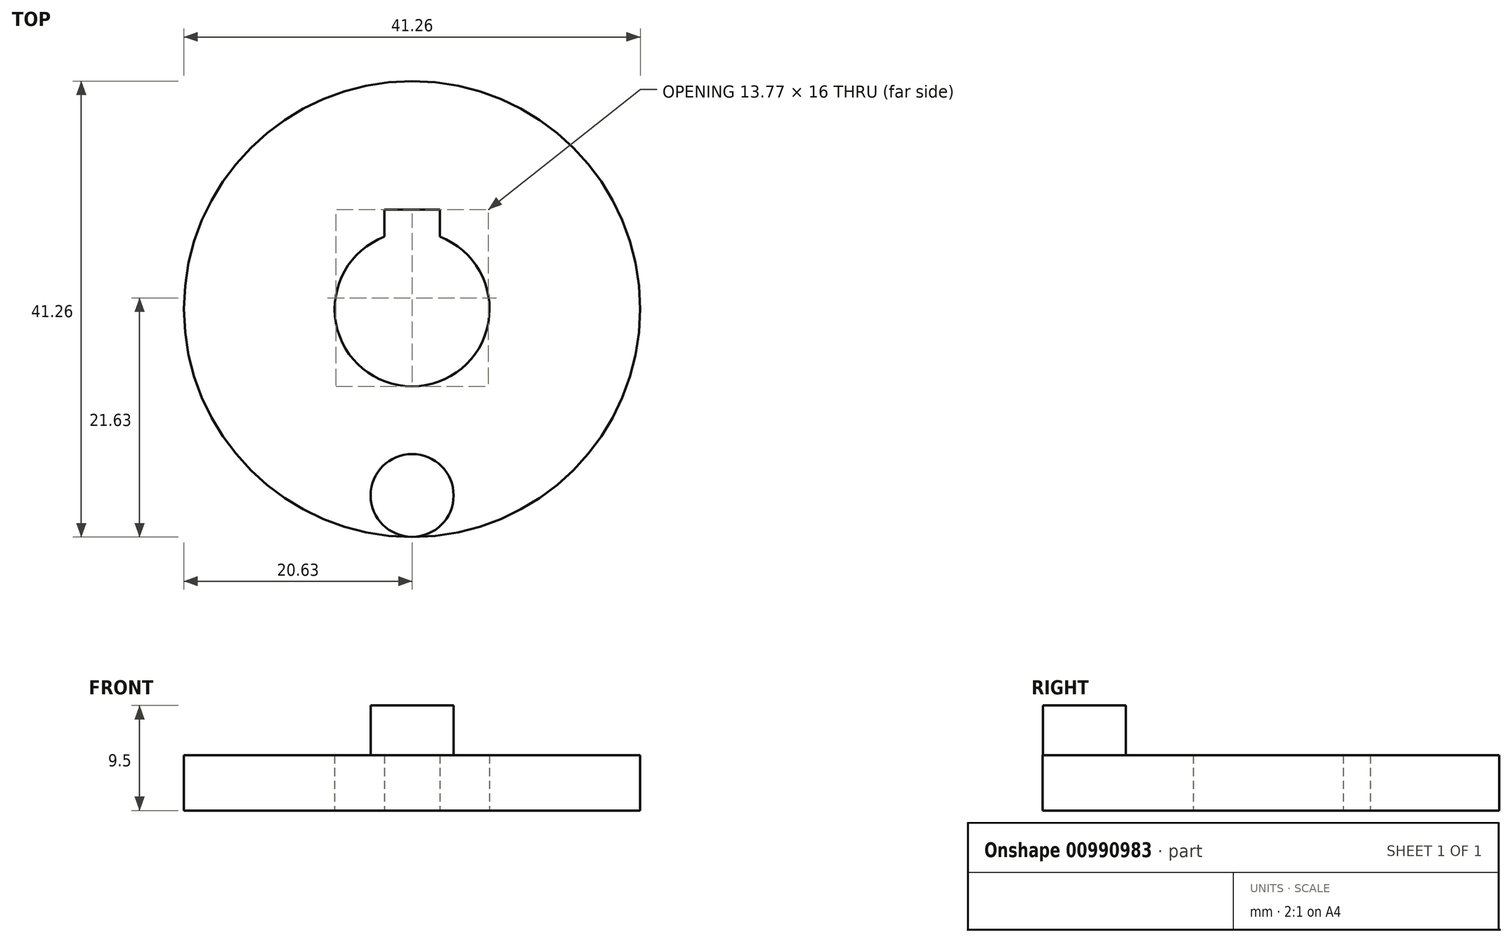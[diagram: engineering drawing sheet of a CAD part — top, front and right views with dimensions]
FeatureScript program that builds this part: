
annotation { "Feature Type Name" : "Feature", "Feature Type Description" : "" }
export const myFeature = defineFeature(function(context is Context, id is Id, definition is map)
    precondition{}
    {
        {
            var Q0;
            Q0=qCreatedBy(makeId("Top.planeOp"),FACE);
            var sketch = newSketch(context, id + "F0", { "sketchPlane" : qUnion([Q0])});
            skCircle(sketch, "E0", {"center": v(0, 0) * mm, "radius": 20.62 * mm});
            skCircle(sketch, "E1", {"center": v(0, 0) * mm, "radius": 7 * mm});
            skLineSegment(sketch, "E2", {"start": v(-2.5, 9) * mm, "end": v(2.5, 9) * mm});
            skLineSegment(sketch, "E3", {"start": v(-2.5, 9) * mm, "end": v(-2.5, 6.54) * mm});
            skLineSegment(sketch, "E4", {"start": v(2.5, 9) * mm, "end": v(2.5, 6.54) * mm});
            skSolve(sketch);
        }
        {
            var Q0;
            Q0=makeQuery(id+"F0.imprint","IMPRINT",FACE,{"disambiguationData":[TD([[makeQuery(id+"F0.imprint","IMPRINT",EDGE,{"derivedFrom":sQuery(id+"F0.wireOp",EDGE,"E0")}),1.0]])]});
            extrude(context, id + "F1", {"entities" : qUnion([Q0]), "depth" : 5 * mm, "offsetDistance" : 25 * mm});
        }
        {
            var Q0;
            Q0=makeQuery(id+"F1.opExtrude","CAP_FACE",FACE,{"disambiguationData":[OSD([sQuery(id+"F0.wireOp",EDGE,"E0"),sQuery(id+"F0.wireOp",EDGE,"E1")])],"isStart":false});
            var sketch = newSketch(context, id + "F2", { "sketchPlane" : qUnion([Q0])});
            skSolve(sketch);
        }
        {
            var Q0;
            Q0=makeQuery(id+"F2.imprint","IMPRINT",FACE,{"disambiguationData":[TD([[makeQuery(id+"F2.imprint","IMPRINT",EDGE,{"derivedFrom":makeQuery(id+"F1.opExtrude","CAP_EDGE",EDGE,{"disambiguationData":[OSD([sQuery(id+"F0.wireOp",EDGE,"E0")])],"isStart":false})}),1.0]])]});
            var sketch = newSketch(context, id + "F3", { "sketchPlane" : qUnion([Q0])});
            skCircle(sketch, "E5", {"center": v(0, -16.87) * mm, "radius": 3.75 * mm});
            skSolve(sketch);
        }
        {
            var Q0;
            Q0=makeQuery(id+"F3.imprint","IMPRINT",FACE,{"disambiguationData":[TD([[makeQuery(id+"F3.imprint","IMPRINT",EDGE,{"derivedFrom":sQuery(id+"F3.wireOp",EDGE,"E5")}),1.0]])]});
            var Q1;
            Q1=sQuery(id+"F3.wireOp",EDGE,"E5");
            extrude(context, id + "F4", {"entities" : qUnion([Q0]), "operationType" : NewBodyOperationType.ADD, "surfaceEntities" : qUnion([Q1]), "depth" : 4.5 * mm, "offsetDistance" : 25 * mm});
        }
    });
